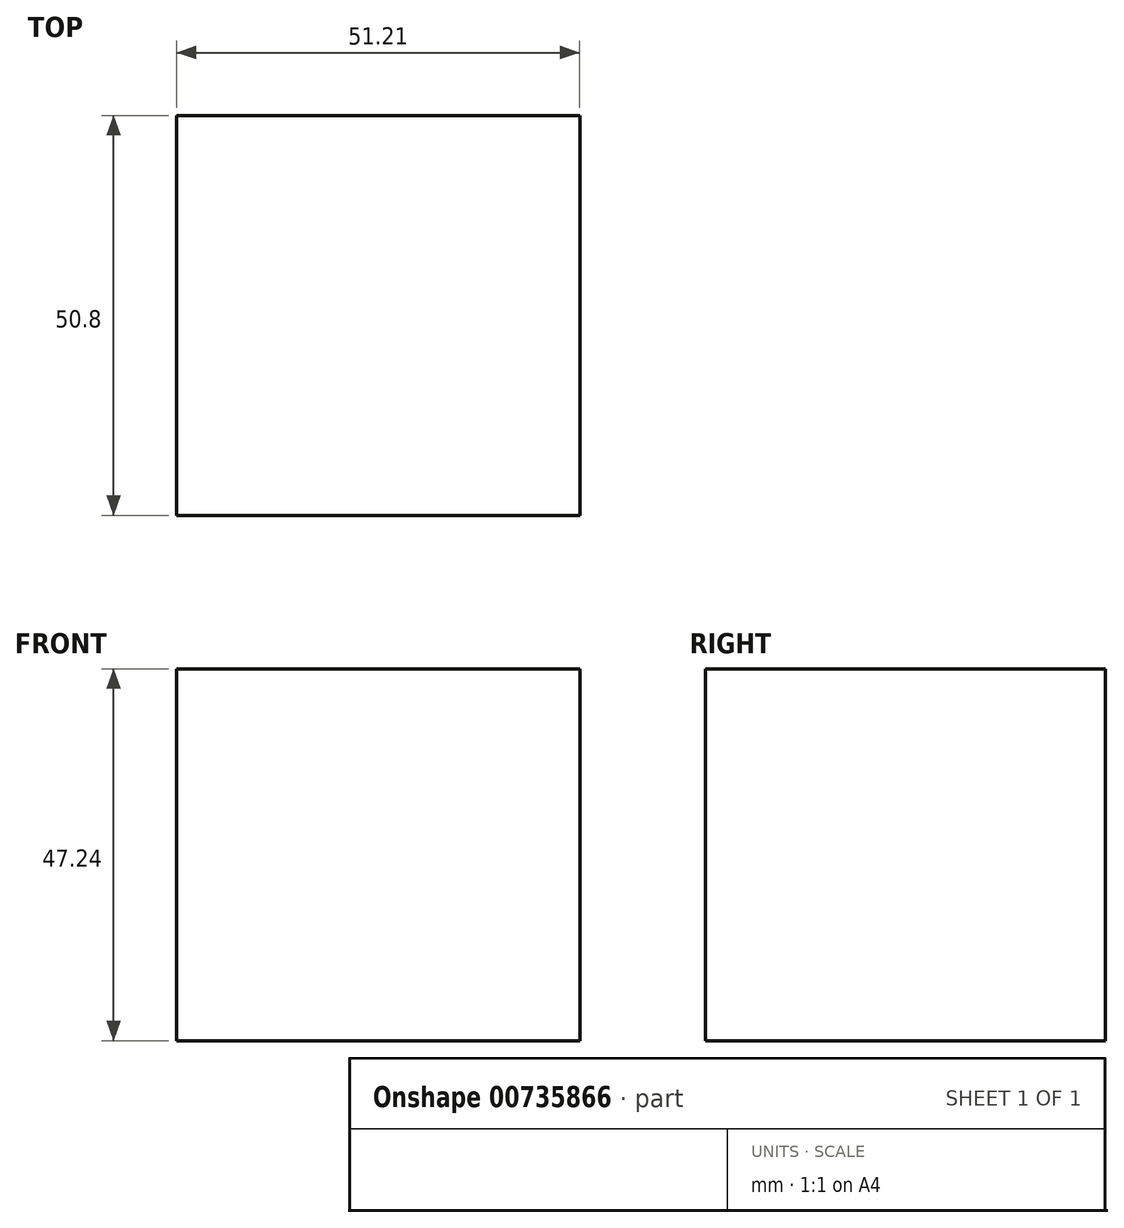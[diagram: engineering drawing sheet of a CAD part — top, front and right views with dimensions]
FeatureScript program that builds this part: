
annotation { "Feature Type Name" : "Feature", "Feature Type Description" : "" }
export const myFeature = defineFeature(function(context is Context, id is Id, definition is map)
    precondition{}
    {
        {
            var Q0;
            Q0=qCreatedBy(makeId("Front.planeOp"),FACE);
            var sketch = newSketch(context, id + "F0", { "sketchPlane" : qUnion([Q0])});
            skLineSegment(sketch, "E0", {"start": v(0, 0) * mm, "end": v(51.21, 0) * mm});
            skLineSegment(sketch, "E1", {"start": v(51.21, 0) * mm, "end": v(51.21, 47.24) * mm});
            skLineSegment(sketch, "E2", {"start": v(51.21, 47.24) * mm, "end": v(0, 47.24) * mm});
            skLineSegment(sketch, "E3", {"start": v(0, 47.24) * mm, "end": v(0, 0) * mm});
            skSolve(sketch);
        }
        {
            var Q0;
            Q0=makeQuery(id+"F0.imprint","IMPRINT",FACE,{"disambiguationData":[TD([[makeQuery(id+"F0.imprint","IMPRINT",EDGE,{"derivedFrom":sQuery(id+"F0.wireOp",EDGE,"E0")}),1.0]])]});
            extrude(context, id + "F1", {"entities" : qUnion([Q0]), "depth" : 50.8 * mm, "offsetDistance" : 25.4 * mm});
        }
    });
